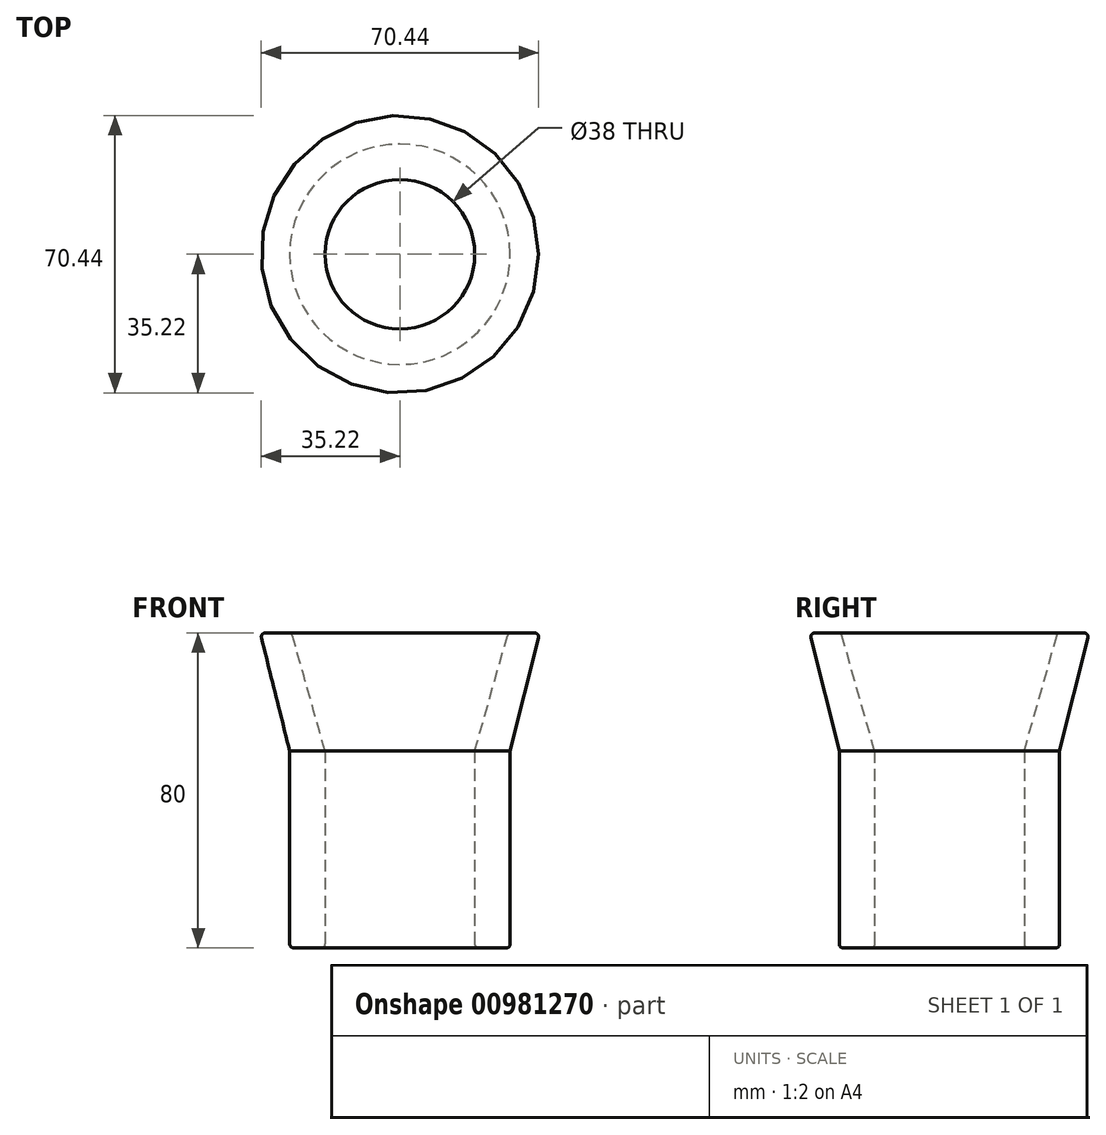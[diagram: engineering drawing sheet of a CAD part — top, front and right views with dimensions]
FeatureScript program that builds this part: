
annotation { "Feature Type Name" : "Feature", "Feature Type Description" : "" }
export const myFeature = defineFeature(function(context is Context, id is Id, definition is map)
    precondition{}
    {
        {
            var Q0;
            Q0=qCreatedBy(makeId("Front.planeOp"),FACE);
            var sketch = newSketch(context, id + "F0", { "sketchPlane" : qUnion([Q0])});
            skLineSegment(sketch, "E0", {"start": v(0, 0) * mm, "end": v(-19, 0) * mm, "construction": true});
            skLineSegment(sketch, "E1", {"start": v(-19, 0) * mm, "end": v(-28, 0) * mm, "construction": true});
            skLineSegment(sketch, "E2", {"start": v(-19, 0) * mm, "end": v(-19, 50) * mm, "construction": true});
            skLineSegment(sketch, "E3", {"start": v(-28, 0) * mm, "end": v(-28, 50) * mm, "construction": true});
            skLineSegment(sketch, "E4", {"start": v(-19, 50) * mm, "end": v(-19, 80) * mm, "construction": true});
            skLineSegment(sketch, "E5", {"start": v(-19, 80) * mm, "end": v(-27.5, 80) * mm, "construction": true});
            skLineSegment(sketch, "E6", {"start": v(-27.5, 80) * mm, "end": v(-35.5, 80) * mm, "construction": true});
            skLineSegment(sketch, "E7", {"start": v(0, 0) * mm, "end": v(0, 122.85) * mm, "construction": true});
            skLineSegment(sketch, "E8", {"start": v(-28, 0) * mm, "end": v(-28, 50) * mm});
            skLineSegment(sketch, "E9", {"start": v(-28, 50) * mm, "end": v(-35.5, 80) * mm});
            skLineSegment(sketch, "E10", {"start": v(-27.5, 80) * mm, "end": v(-19, 50) * mm});
            skLineSegment(sketch, "E11", {"start": v(-19, 50) * mm, "end": v(-19, 0) * mm});
            skLineSegment(sketch, "E12", {"start": v(-19, 0) * mm, "end": v(-28, 0) * mm});
            skLineSegment(sketch, "E13", {"start": v(-35.5, 80) * mm, "end": v(-27.5, 80) * mm});
            skSolve(sketch);
        }
        {
            var Q0;
            Q0=makeQuery(id+"F0.imprint","IMPRINT",FACE,{"disambiguationData":[TD([[makeQuery(id+"F0.imprint","IMPRINT",EDGE,{"derivedFrom":sQuery(id+"F0.wireOp",EDGE,"E8")}),-1.0]])]});
            var Q1;
            Q1=sQuery(id+"F0.wireOp",EDGE,"E7");
            revolve(context, id + "F1", {"surfaceOperationType" : NewSurfaceOperationType.NEW, "entities" : qUnion([Q0]), "axis" : qUnion([Q1]), "revolveType" : RevolveType.FULL});
        }
        {
            var Q0;
            Q0=makeQuery(id+"F1.opRevolve","SWEPT_EDGE",EDGE,{"disambiguationData":[OSD([sQuery(id+"F0.wireOp",EDGE,"E10"),sQuery(id+"F0.wireOp",EDGE,"E13")])]});
            fillet(context, id + "F2", {"entities" : qUnion([Q0]), "radius" : 1 * mm, "tangentPropagation" : true, "allowEdgeOverflow" : false});
        }
        {
            var Q0;
            Q0=makeQuery(id+"F1.opRevolve","SWEPT_EDGE",EDGE,{"disambiguationData":[OSD([sQuery(id+"F0.wireOp",EDGE,"E9"),sQuery(id+"F0.wireOp",EDGE,"E13")])]});
            var Q1;
            Q1=makeQuery(id+"F1.opRevolve","SWEPT_EDGE",EDGE,{"disambiguationData":[OSD([sQuery(id+"F0.wireOp",EDGE,"E8"),sQuery(id+"F0.wireOp",EDGE,"E12")])]});
            var Q2;
            Q2=makeQuery(id+"F1.opRevolve","SWEPT_EDGE",EDGE,{"disambiguationData":[OSD([sQuery(id+"F0.wireOp",EDGE,"E11"),sQuery(id+"F0.wireOp",EDGE,"E12")])]});
            fillet(context, id + "F3", {"entities" : qUnion([Q0, Q1, Q2]), "radius" : 1 * mm, "tangentPropagation" : true, "allowEdgeOverflow" : false});
        }
    });
